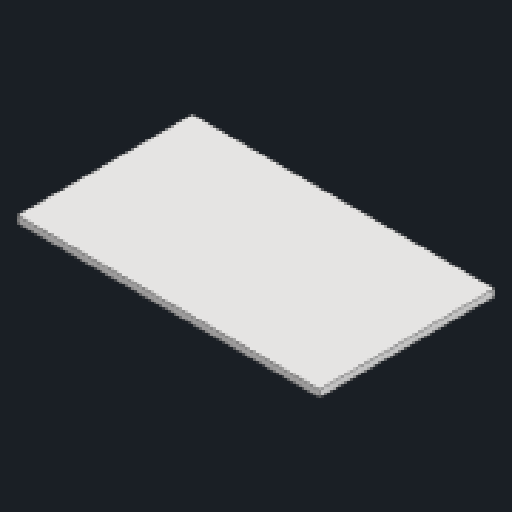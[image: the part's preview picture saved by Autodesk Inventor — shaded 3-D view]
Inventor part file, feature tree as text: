
AUTODESK INVENTOR PART (.ipt)
format: ipt  version: 2023 (Build 270158000, 158)  size: 124,416 bytes
history: native  units: mm
features: extrude x2, sketch x2
ambient origin geometry x8: Origin, YZ Plane, XZ Plane, XY Plane, X Axis, Y Axis, Z Axis, Center Point
bodies: Solid1 (feature_tree)
feature tree (4):
  extrude  "Extrusion1"  Depth=73.0mm
  extrude  "Extrusion3"  Depth=10.0mm TaperAngle=0.0deg
  sketch  "Sketch1"  dims[d0=126.0mm d1=73.0mm]
  sketch  "Sketch3"  dims[d2=3.0mm d3=0.0mm d6=10.0mm d7=0.0mm]
